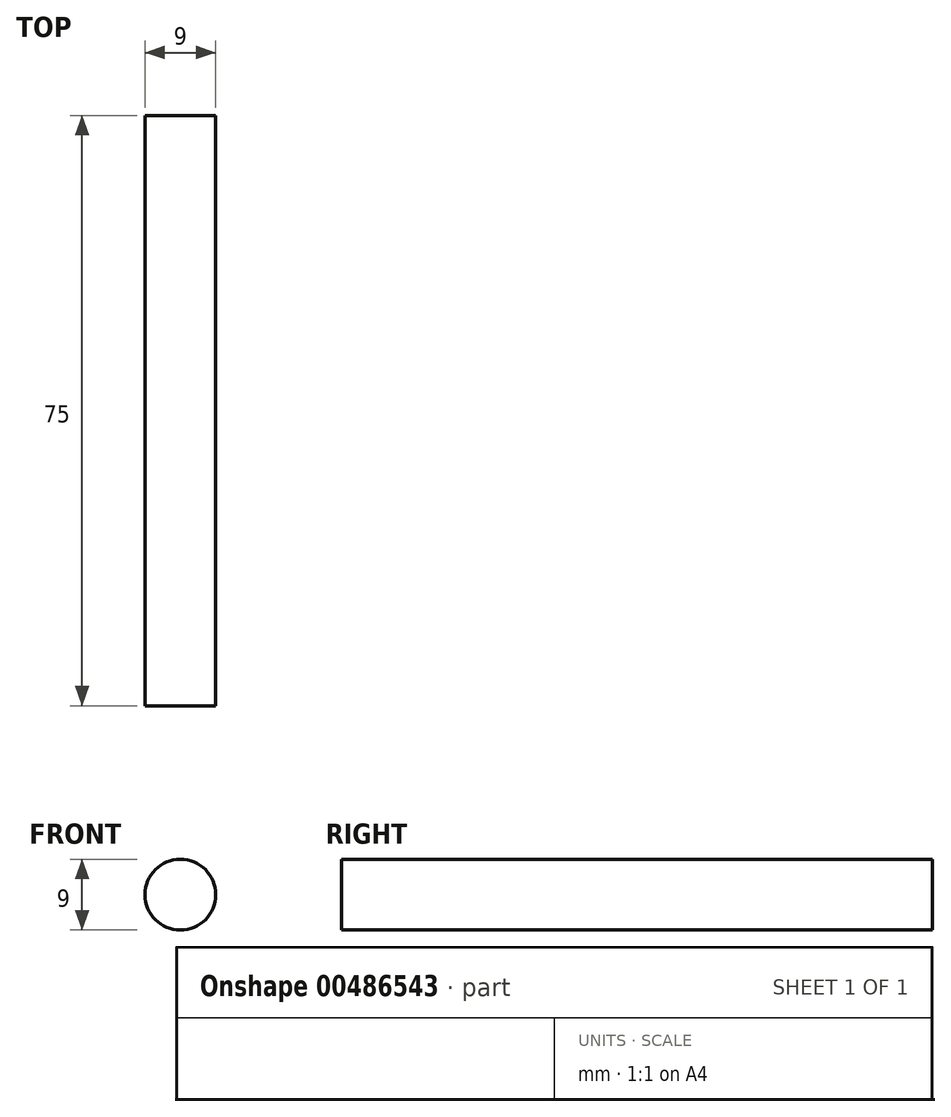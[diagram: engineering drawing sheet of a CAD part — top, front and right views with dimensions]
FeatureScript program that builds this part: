
annotation { "Feature Type Name" : "Feature", "Feature Type Description" : "" }
export const myFeature = defineFeature(function(context is Context, id is Id, definition is map)
    precondition{}
    {
        {
            var Q0;
            Q0=qCreatedBy(makeId("Front.planeOp"),FACE);
            var sketch = newSketch(context, id + "F0", { "sketchPlane" : qUnion([Q0])});
            skCircle(sketch, "E0", {"center": v(0, 0) * mm, "radius": 4.5 * mm});
            skSolve(sketch);
        }
        {
            var Q0;
            Q0 = qSketchRegion(id + "F0", true);
            extrude(context, id + "F1", {"entities" : qUnion([Q0]), "oppositeDirection" : true, "depth" : 75 * mm, "offsetDistance" : 25 * mm});
        }
    });
